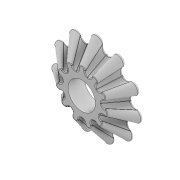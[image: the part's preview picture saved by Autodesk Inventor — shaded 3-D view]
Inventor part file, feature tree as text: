
AUTODESK INVENTOR PART (.ipt)
format: ipt  version: 2020 (Build 240168000, 168)  size: 969,728 bytes
history: native  units: in
note: dims shown in document units (in); Inventor stores cm internally (conversion verified against a paired STEP export)
features: sketch x3, plane x1, loft x1, extrude x1, fillet x1
ambient origin geometry x8: Origin, YZ Plane, XZ Plane, XY Plane, X Axis, Y Axis, Z Axis, Center Point
bodies: Solid1 (feature_tree)
feature tree (7):
  sketch  "Sketch1"  dims[d0=0.1969in d1=0.1575in]
  plane  "Work Plane1"
  loft  "Loft1"
  extrude  "Extrusion1"  Depth=0.0827in
  fillet  "Fillet1"  Radius=0.0827in
  sketch  "Sketch3"  dims[d2=0.0866in d3=0.0827in d4=0.0827in]
  sketch  "Sketch4"  dims[d5=0.0827in d6=4.3307in d8=360.0deg d10=0.1181in d18=4.3307in d20=360.0deg d22=0.0in d23=90.0deg d24=0.0in d25=90.0deg d26=0.1969in d27=1.0in d28=0.0in d29=0.0079in]
